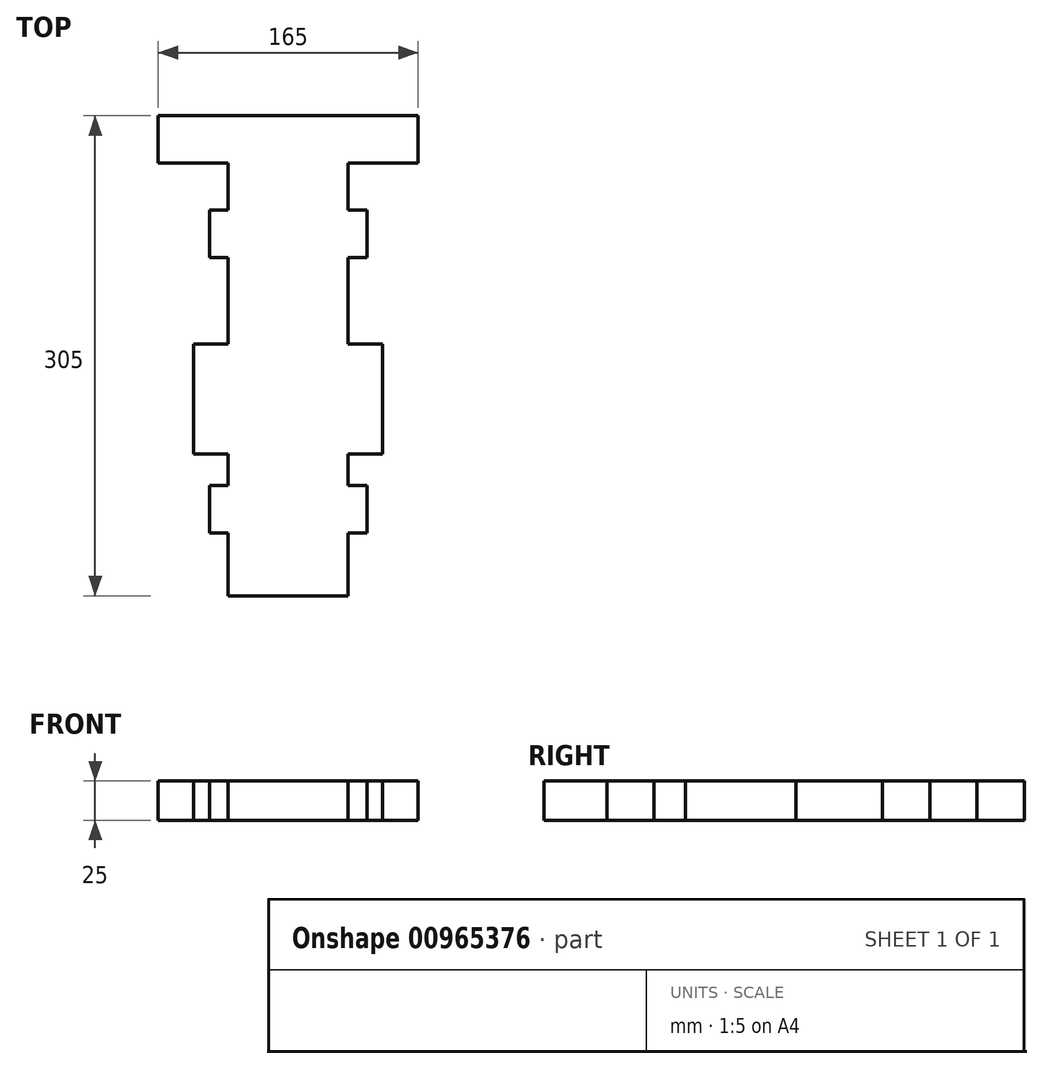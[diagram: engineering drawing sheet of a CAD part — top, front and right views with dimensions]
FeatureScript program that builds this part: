
annotation { "Feature Type Name" : "Feature", "Feature Type Description" : "" }
export const myFeature = defineFeature(function(context is Context, id is Id, definition is map)
    precondition{}
    {
        {
            var Q0;
            Q0=qCreatedBy(makeId("Top.planeOp"),FACE);
            var sketch = newSketch(context, id + "F0", { "sketchPlane" : qUnion([Q0])});
            skLineSegment(sketch, "E0.bottom", {"start": v(-10.32, 240.3) * mm, "end": v(65.68, 240.3) * mm});
            skLineSegment(sketch, "E0.top", {"start": v(-10.32, -64.7) * mm, "end": v(65.68, -64.7) * mm});
            skLineSegment(sketch, "E0.left", {"start": v(-10.32, 240.3) * mm, "end": v(-10.32, -64.7) * mm});
            skLineSegment(sketch, "E0.right", {"start": v(65.68, 240.3) * mm, "end": v(65.68, -64.7) * mm});
            skLineSegment(sketch, "E1.bottom", {"start": v(-54.82, 240.3) * mm, "end": v(110.18, 240.3) * mm});
            skLineSegment(sketch, "E1.top", {"start": v(-54.82, 210.3) * mm, "end": v(110.18, 210.3) * mm});
            skLineSegment(sketch, "E1.left", {"start": v(-54.82, 240.3) * mm, "end": v(-54.82, 210.3) * mm});
            skLineSegment(sketch, "E1.right", {"start": v(110.18, 240.3) * mm, "end": v(110.18, 210.3) * mm});
            skPoint(sketch, "E2", {"position": v(27.68, 240.3) * mm});
            skLineSegment(sketch, "E3.bottom", {"start": v(-32.32, 95.3) * mm, "end": v(87.68, 95.3) * mm});
            skLineSegment(sketch, "E3.top", {"start": v(-32.32, 25.3) * mm, "end": v(87.68, 25.3) * mm});
            skLineSegment(sketch, "E3.left", {"start": v(-32.32, 95.3) * mm, "end": v(-32.32, 25.3) * mm});
            skLineSegment(sketch, "E3.right", {"start": v(87.68, 95.3) * mm, "end": v(87.68, 25.3) * mm});
            skPoint(sketch, "E4", {"position": v(27.68, 95.3) * mm});
            skPoint(sketch, "E5", {"position": v(65.68, 25.3) * mm});
            skLineSegment(sketch, "E6.bottom", {"start": v(-22.32, 180.3) * mm, "end": v(77.68, 180.3) * mm});
            skLineSegment(sketch, "E6.top", {"start": v(-22.32, 150.3) * mm, "end": v(77.68, 150.3) * mm});
            skLineSegment(sketch, "E6.left", {"start": v(-22.32, 180.3) * mm, "end": v(-22.32, 150.3) * mm});
            skLineSegment(sketch, "E6.right", {"start": v(77.68, 180.3) * mm, "end": v(77.68, 150.3) * mm});
            skPoint(sketch, "E7", {"position": v(27.68, 180.3) * mm});
            skPoint(sketch, "E8", {"position": v(65.68, 180.3) * mm});
            skLineSegment(sketch, "E9.bottom", {"start": v(-22.32, 5.3) * mm, "end": v(77.68, 5.3) * mm});
            skLineSegment(sketch, "E9.top", {"start": v(-22.32, -24.7) * mm, "end": v(77.68, -24.7) * mm});
            skLineSegment(sketch, "E9.left", {"start": v(-22.32, 5.3) * mm, "end": v(-22.32, -24.7) * mm});
            skLineSegment(sketch, "E9.right", {"start": v(77.68, 5.3) * mm, "end": v(77.68, -24.7) * mm});
            skPoint(sketch, "E10", {"position": v(27.68, 5.3) * mm});
            skPoint(sketch, "E11", {"position": v(65.68, -24.7) * mm});
            skSolve(sketch);
        }
        {
            var Q0;
            Q0 = qSketchRegion(id + "F0", true);
            extrude(context, id + "F1", {"entities" : qUnion([Q0]), "depth" : 25 * mm, "offsetDistance" : 25 * mm});
        }
    });
